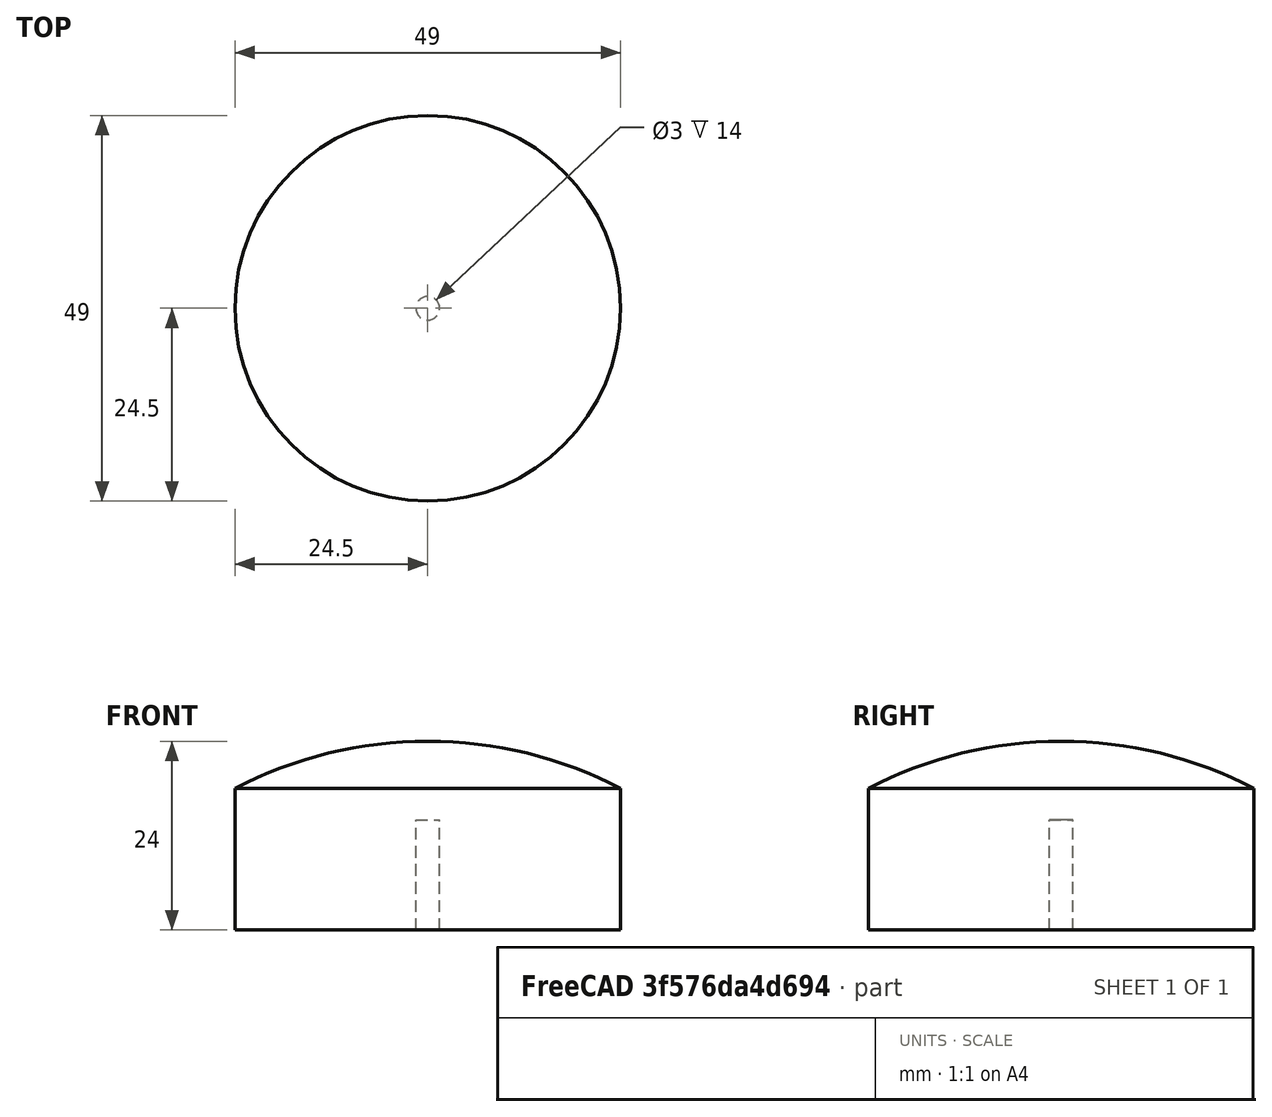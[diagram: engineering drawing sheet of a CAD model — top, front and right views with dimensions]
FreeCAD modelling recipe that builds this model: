
FCSTD DOCUMENT  (FreeCAD 0.18.4R)
Label: 6
License: All rights reserved
LicenseURL: http://en.wikipedia.org/wiki/All_rights_reserved
objects: Sketcher::SketchObject×1, PartDesign::Revolution×1, PartDesign::Body×1
note: 4 computed .brp shape members not serialized (recipe doc carries the construction recipe); baked Part::Feature solids carry a one-line shape summary decoded from their .brp

FEATURE [Sketcher::SketchObject] Sketch
  MapMode = 5
  Placement = pos=(0,0,0) rot=(1,0,0;1.5708rad)
  Support = -> [XZ_Plane]
  constraints (19):
    c: PointOnObject(g0,g-2)
    c: PointOnObject(g0,g-2)
    c: Coincident(g1,g0)
    c: PointOnObject(g1,g-1)
    c: Vertical(g1)
    c: Coincident(g2,g1)
    c: PointOnObject(g2,g-1)
    c: Coincident(g3,g2)
    c: Vertical(g3)
    c: Coincident(g4,g3)
    c: Horizontal(g4)
    c: Coincident(g5,g4)
    c: Coincident(g5,g0)
    c: Vertical(g5)
    c: Distance(g1,g-1) = 24.5
    c: Distance(g1) = 18
    c: Distance(g0,g-1) = 24
    c: Distance(g4) = 1.5
    c: Distance(g0,g4) = 10
FEATURE [PartDesign::Revolution] Revolution
  Angle = 360
  Axis = (0,2e-16,1)
  Base = (0,0,0)
  Placement = pos=(0,0,0) rot=(1,0,0;1.5708rad)
  Profile = -> Sketch
  ReferenceAxis = -> Sketch [V_Axis]
FEATURE [PartDesign::Body] Body
  Group = -> [Sketch,Revolution]
  Origin = -> Origin
  Tip = -> Revolution
